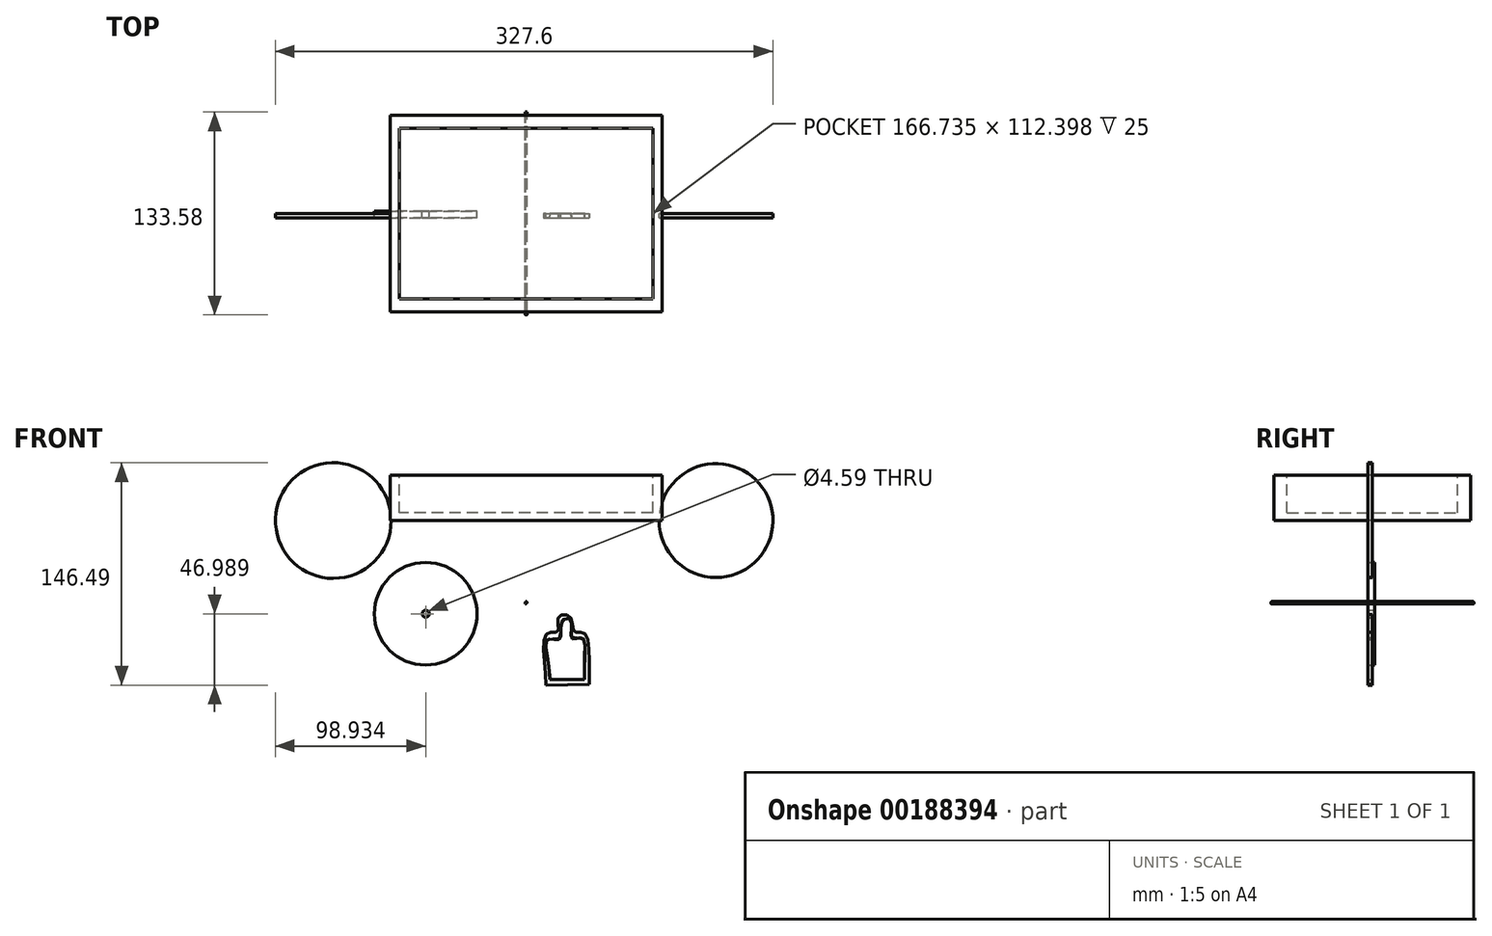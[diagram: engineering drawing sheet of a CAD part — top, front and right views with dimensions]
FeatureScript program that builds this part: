
annotation { "Feature Type Name" : "Feature", "Feature Type Description" : "" }
export const myFeature = defineFeature(function(context is Context, id is Id, definition is map)
    precondition{}
    {
        {
            var Q0;
            Q0=qCreatedBy(makeId("Front.planeOp"),FACE);
            var sketch = newSketch(context, id + "F0", { "sketchPlane" : qUnion([Q0])});
            skCircle(sketch, "E0", {"center": v(-127, 0) * mm, "radius": 38.1 * mm});
            skCircle(sketch, "E1", {"center": v(125, 0) * mm, "radius": 37.5 * mm});
            skCircle(sketch, "E2", {"center": v(-66.17, -61.4) * mm, "radius": 33.8 * mm});
            skCircle(sketch, "E3", {"center": v(-66.17, -61.4) * mm, "radius": 2.3 * mm});
            skFitSpline(sketch, "E4", {"points": [v(13.1, -108.39) * mm, v(13.55, -74.6) * mm, v(20.74, -72.96) * mm, v(21.44, -63.44) * mm, v(29.2, -63.79) * mm, v(31.67, -73.31) * mm, v(38.44, -74.16) * mm, v(41.55, -107.95) * mm], "startDerivative": vector(0, 155.32) * mm, "endDerivative": vector(6.66, -159.73) * mm});
            skLineSegment(sketch, "E5", {"start": v(13.1, -108.39) * mm, "end": v(41.55, -107.95) * mm});
            skFitSpline(sketch, "E6", {"points": [v(38.36, -104.64) * mm, v(36.6, -77.19) * mm, v(30.26, -77.9) * mm, v(29.2, -65.2) * mm, v(23.56, -66.6) * mm, v(22.15, -77.9) * mm, v(14.39, -78.25) * mm, v(15.8, -104.7) * mm], "startDerivative": vector(-10.08, 191.55) * mm, "endDerivative": vector(10.08, -201.53) * mm});
            skLineSegment(sketch, "E7", {"start": v(15.8, -104.7) * mm, "end": v(38.36, -104.64) * mm});
            skSolve(sketch);
        }
        {
            var Q0;
            Q0 = qSketchRegion(id + "F0", true);
            extrude(context, id + "F1", {"entities" : qUnion([Q0]), "depth" : 3 * mm});
        }
        {
            var Q0;
            Q0=qCreatedBy(makeId("Top.planeOp"),FACE);
            var sketch = newSketch(context, id + "F2", { "sketchPlane" : qUnion([Q0])});
            skLineSegment(sketch, "E8.bottom", {"start": v(89.54, 64.8) * mm, "end": v(-89.54, 64.8) * mm});
            skLineSegment(sketch, "E8.top", {"start": v(89.54, -64.8) * mm, "end": v(-89.54, -64.8) * mm});
            skLineSegment(sketch, "E8.left", {"start": v(89.54, 64.8) * mm, "end": v(89.54, -64.8) * mm});
            skLineSegment(sketch, "E8.right", {"start": v(-89.54, 64.8) * mm, "end": v(-89.54, -64.8) * mm});
            skPoint(sketch, "E8.middle", {"position": v(0, 0) * mm});
            skSolve(sketch);
        }
        {
            var Q0;
            Q0 = qSketchRegion(id + "F2", true);
            extrude(context, id + "F3", {"entities" : qUnion([Q0]), "depth" : 30 * mm});
        }
        {
            var Q0;
            Q0=makeQuery(id+"F3.opExtrude","CAP_FACE",FACE,{"disambiguationData":[OSD([sQuery(id+"F2.wireOp",EDGE,"E8.bottom"),sQuery(id+"F2.wireOp",EDGE,"E8.top"),sQuery(id+"F2.wireOp",EDGE,"E8.left"),sQuery(id+"F2.wireOp",EDGE,"E8.right")])],"isStart":false});
            var sketch = newSketch(context, id + "F4", { "sketchPlane" : qUnion([Q0])});
            skLineSegment(sketch, "E9.bottom", {"start": v(83.37, -56.2) * mm, "end": v(-83.37, -56.2) * mm});
            skLineSegment(sketch, "E9.top", {"start": v(83.37, 56.2) * mm, "end": v(-83.37, 56.2) * mm});
            skLineSegment(sketch, "E9.left", {"start": v(83.37, -56.2) * mm, "end": v(83.37, 56.2) * mm});
            skLineSegment(sketch, "E9.right", {"start": v(-83.37, -56.2) * mm, "end": v(-83.37, 56.2) * mm});
            skPoint(sketch, "E9.middle", {"position": v(0, 0) * mm});
            skSolve(sketch);
        }
        {
            var Q0;
            Q0=makeQuery(id+"F4.imprint","IMPRINT",FACE,{"disambiguationData":[TD([[makeQuery(id+"F4.imprint","IMPRINT",EDGE,{"derivedFrom":sQuery(id+"F4.wireOp",EDGE,"E9.bottom")}),-1.0]])]});
            extrude(context, id + "F5", {"entities" : qUnion([Q0]), "operationType" : NewBodyOperationType.REMOVE, "oppositeDirection" : true, "depth" : 25 * mm});
        }
        {
            var Q0;
            Q0=qCreatedBy(makeId("Right.planeOp"),FACE);
            var sketch = newSketch(context, id + "F6", { "sketchPlane" : qUnion([Q0])});
            skLineSegment(sketch, "E10.bottom", {"start": v(-66.8, -53.15) * mm, "end": v(66.8, -53.15) * mm});
            skLineSegment(sketch, "E10.top", {"start": v(-66.8, -54.89) * mm, "end": v(66.8, -54.89) * mm});
            skLineSegment(sketch, "E10.left", {"start": v(-66.8, -53.15) * mm, "end": v(-66.8, -54.89) * mm});
            skLineSegment(sketch, "E10.right", {"start": v(66.8, -53.15) * mm, "end": v(66.8, -54.89) * mm});
            skPoint(sketch, "E10.middle", {"position": v(0, -54.02) * mm});
            skSolve(sketch);
        }
        {
            var Q0;
            Q0 = qSketchRegion(id + "F6", true);
            extrude(context, id + "F7", {"entities" : qUnion([Q0]), "endBound" : BoundingType.SYMMETRIC, "depth" : 1 * mm});
        }
        {
            var Q0;
            Q0=makeQuery(id+"F7.opExtrude","CAP_EDGE",EDGE,{"disambiguationData":[OSD([sQuery(id+"F6.wireOp",EDGE,"E10.bottom")])],"isStart":false});
            var Q1;
            Q1=makeQuery(id+"F7.opExtrude","SWEPT_FACE",FACE,{"disambiguationData":[OSD([sQuery(id+"F6.wireOp",EDGE,"E10.bottom")])]});
            fillet(context, id + "F8", {"entities" : qUnion([Q0, Q1]), "radius" : 1 * mm, "tangentPropagation" : true, "allowEdgeOverflow" : false});
        }
        {
            var Q0;
            Q0=makeQuery(id+"F7.opExtrude","CAP_EDGE",EDGE,{"disambiguationData":[OSD([sQuery(id+"F6.wireOp",EDGE,"E10.top")])],"isStart":false});
            fillet(context, id + "F9", {"entities" : qUnion([Q0]), "radius" : 1 * mm, "tangentPropagation" : true, "allowEdgeOverflow" : false});
        }
        {
            var Q0;
            Q0=makeQuery(id+"F7.opExtrude","CAP_EDGE",EDGE,{"disambiguationData":[OSD([sQuery(id+"F6.wireOp",EDGE,"E10.top")])],"isStart":true});
            fillet(context, id + "F10", {"entities" : qUnion([Q0]), "radius" : 1 * mm, "tangentPropagation" : true, "allowEdgeOverflow" : false});
        }
        {
            var Q0;
            Q0=makeQuery(id+"F0.imprint","IMPRINT",FACE,{"disambiguationData":[TD([[makeQuery(id+"F0.imprint","IMPRINT",EDGE,{"derivedFrom":sQuery(id+"F0.wireOp",EDGE,"E2")}),1.0]])]});
            extrude(context, id + "F11", {"entities" : qUnion([Q0]), "operationType" : NewBodyOperationType.ADD, "endBound" : BoundingType.SYMMETRIC, "depth" : 3 * mm});
        }
        {
            var Q0;
            Q0=sQuery(id+"F0.wireOp",EDGE,"E3");
            extrude(context, id + "F12", {"bodyType" : ToolBodyType.SURFACE, "operationType" : NewBodyOperationType.REMOVE, "surfaceEntities" : qUnion([Q0]), "endBound" : BoundingType.SYMMETRIC, "oppositeDirection" : true, "depth" : 25 * mm});
        }
        {
            var Q0;
            Q0=makeQuery(id+"F0.imprint","IMPRINT",FACE,{"disambiguationData":[TD([[makeQuery(id+"F0.imprint","IMPRINT",EDGE,{"derivedFrom":sQuery(id+"F0.wireOp",EDGE,"E6")}),1.0]])]});
            extrude(context, id + "F13", {"entities" : qUnion([Q0]), "operationType" : NewBodyOperationType.REMOVE, "depth" : 10 * mm, "hasDraft" : true, "draftAngle" : 3 * degree});
        }
    });
